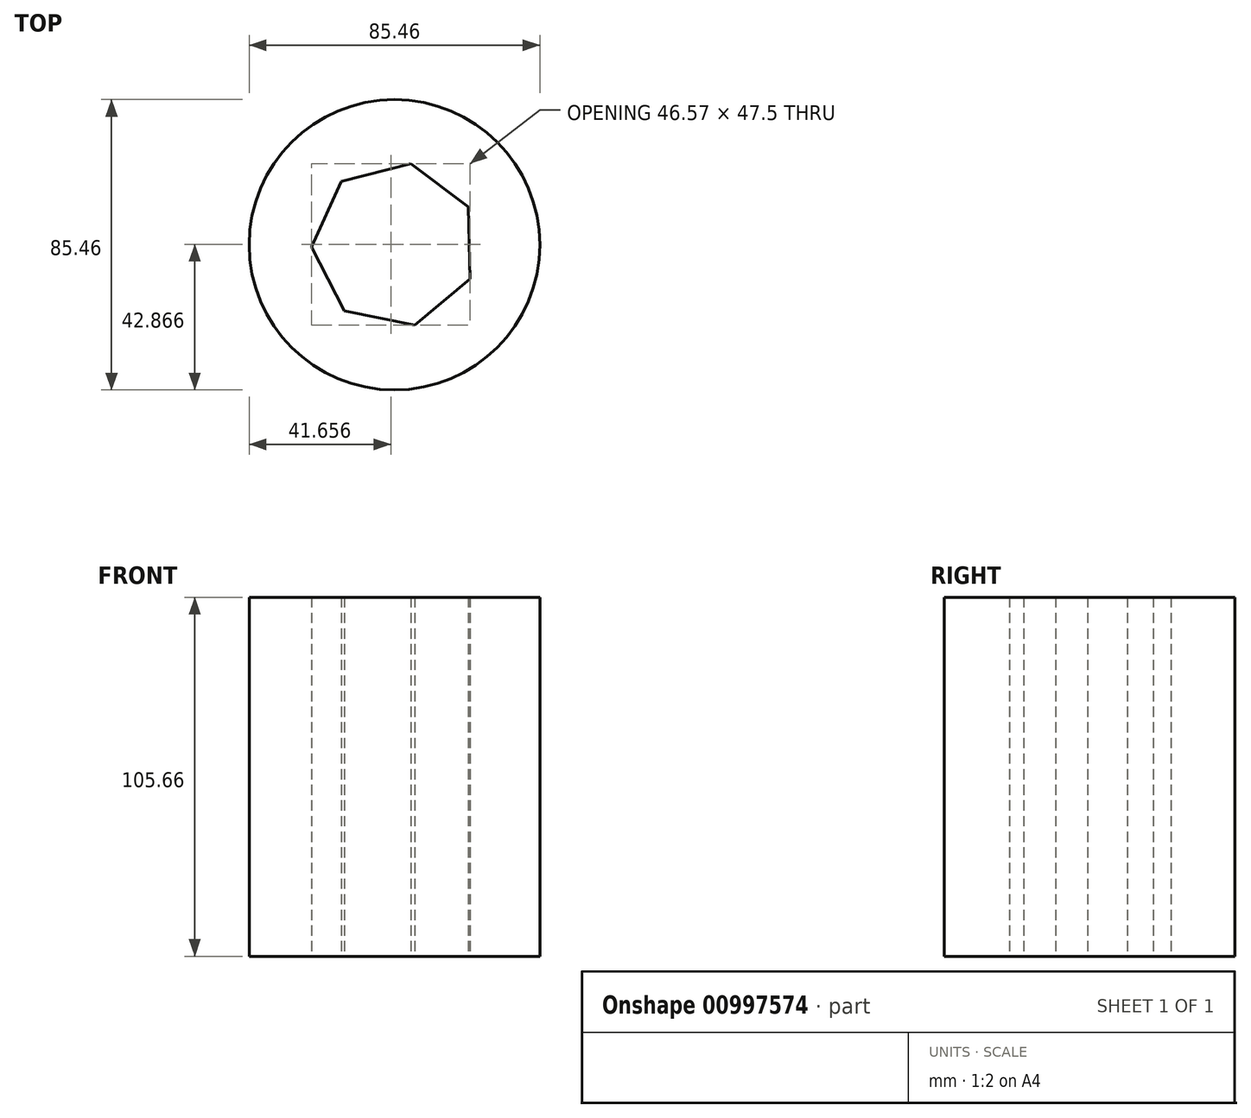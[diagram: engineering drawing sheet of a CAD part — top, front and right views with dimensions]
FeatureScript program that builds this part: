
annotation { "Feature Type Name" : "Feature", "Feature Type Description" : "" }
export const myFeature = defineFeature(function(context is Context, id is Id, definition is map)
    precondition{}
    {
        {
            var Q0;
            Q0=qCreatedBy(makeId("Top.planeOp"),FACE);
            var sketch = newSketch(context, id + "F0", { "sketchPlane" : qUnion([Q0])});
            skCircle(sketch, "E0", {"center": v(0, 0) * mm, "radius": 42.73 * mm});
            skSolve(sketch);
        }
        {
            var Q0;
            Q0 = qSketchRegion(id + "F0", true);
            extrude(context, id + "F1", {"entities" : qUnion([Q0]), "depth" : 105.66 * mm, "offsetDistance" : 25.4 * mm});
        }
        {
            var Q0;
            Q0=qCreatedBy(makeId("Top.planeOp"),FACE);
            var sketch = newSketch(context, id + "F2", { "sketchPlane" : qUnion([Q0])});
            skCircle(sketch, "E1.cCircle", {"center": v(0, 0) * mm, "radius": 21.95 * mm, "construction": true});
            skLineSegment(sketch, "E1.0", {"start": v(-15.66, 18.66) * mm, "end": v(4.83, 23.88) * mm});
            skLineSegment(sketch, "E1.1", {"start": v(4.83, 23.88) * mm, "end": v(21.68, 11.12) * mm});
            skLineSegment(sketch, "E1.2", {"start": v(21.68, 11.12) * mm, "end": v(22.21, -10.02) * mm});
            skLineSegment(sketch, "E1.3", {"start": v(22.21, -10.02) * mm, "end": v(6.01, -23.61) * mm});
            skLineSegment(sketch, "E1.4", {"start": v(6.01, -23.61) * mm, "end": v(-14.71, -19.42) * mm});
            skLineSegment(sketch, "E1.5", {"start": v(-14.71, -19.42) * mm, "end": v(-24.36, -0.6) * mm});
            skLineSegment(sketch, "E1.6", {"start": v(-24.36, -0.6) * mm, "end": v(-15.66, 18.66) * mm});
            skPoint(sketch, "E1.0.midPoint", {"position": v(-5.42, 21.27) * mm});
            skSolve(sketch);
        }
        {
            var Q0;
            Q0 = qSketchRegion(id + "F2", true);
            extrude(context, id + "F3", {"entities" : qUnion([Q0]), "operationType" : NewBodyOperationType.REMOVE, "endBound" : BoundingType.THROUGH_ALL, "depth" : 25.4 * mm, "offsetDistance" : 25.4 * mm});
        }
    });
